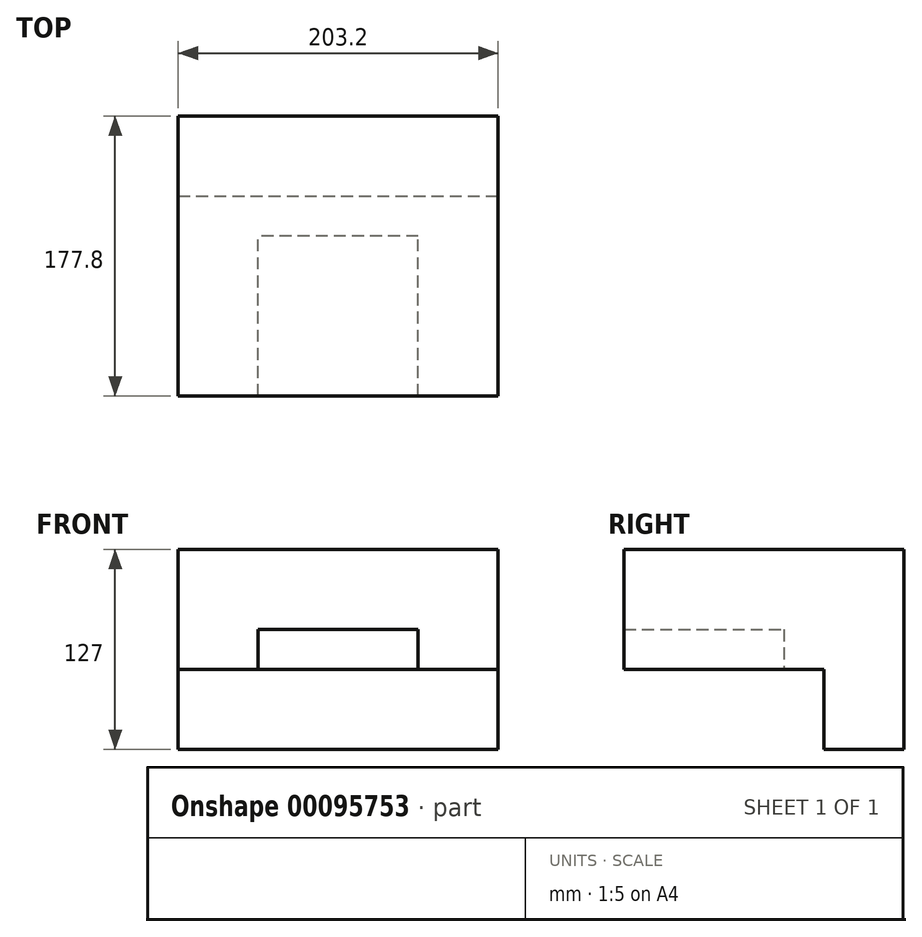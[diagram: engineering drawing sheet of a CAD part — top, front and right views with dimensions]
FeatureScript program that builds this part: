
annotation { "Feature Type Name" : "Feature", "Feature Type Description" : "" }
export const myFeature = defineFeature(function(context is Context, id is Id, definition is map)
    precondition{}
    {
        {
            var Q0;
            Q0=qCreatedBy(makeId("Front.planeOp"),FACE);
            var sketch = newSketch(context, id + "F0", { "sketchPlane" : qUnion([Q0])});
            skLineSegment(sketch, "E0.bottom", {"start": v(-127.89, 75.16) * mm, "end": v(75.31, 75.16) * mm});
            skLineSegment(sketch, "E0.top", {"start": v(-127.89, -51.84) * mm, "end": v(75.31, -51.84) * mm});
            skLineSegment(sketch, "E0.left", {"start": v(-127.89, 75.16) * mm, "end": v(-127.89, -51.84) * mm});
            skLineSegment(sketch, "E0.right", {"start": v(75.31, 75.16) * mm, "end": v(75.31, -51.84) * mm});
            skSolve(sketch);
        }
        {
            var Q0;
            Q0 = qSketchRegion(id + "F0", true);
            extrude(context, id + "F1", {"entities" : qUnion([Q0]), "depth" : 50.8 * mm});
        }
        {
            var Q0;
            Q0=makeQuery(id+"F1.opExtrude","CAP_FACE",FACE,{"disambiguationData":[OSD([sQuery(id+"F0.wireOp",EDGE,"E0.bottom"),sQuery(id+"F0.wireOp",EDGE,"E0.top"),sQuery(id+"F0.wireOp",EDGE,"E0.left"),sQuery(id+"F0.wireOp",EDGE,"E0.right")])],"isStart":false});
            var sketch = newSketch(context, id + "F2", { "sketchPlane" : qUnion([Q0])});
            skLineSegment(sketch, "E1", {"start": v(-127.89, -1.04) * mm, "end": v(75.31, -1.04) * mm});
            skLineSegment(sketch, "E2.bottom", {"start": v(-127.89, 75.16) * mm, "end": v(75.31, 75.16) * mm});
            skLineSegment(sketch, "E2.left", {"start": v(-127.89, 75.16) * mm, "end": v(-127.89, -1.04) * mm});
            skLineSegment(sketch, "E2.right", {"start": v(75.31, 75.16) * mm, "end": v(75.31, -1.04) * mm});
            skSolve(sketch);
        }
        {
            var Q0;
            Q0 = qSketchRegion(id + "F2", true);
            extrude(context, id + "F3", {"entities" : qUnion([Q0]), "operationType" : NewBodyOperationType.ADD, "depth" : 25.4 * mm});
        }
        {
            var Q0;
            Q0=makeQuery(id+"F3.opExtrude","CAP_FACE",FACE,{"disambiguationData":[OSD([sQuery(id+"F2.wireOp",EDGE,"E2.bottom"),sQuery(id+"F2.wireOp",EDGE,"E1"),sQuery(id+"F2.wireOp",EDGE,"E2.left"),sQuery(id+"F2.wireOp",EDGE,"E2.right")])],"isStart":false});
            var sketch = newSketch(context, id + "F4", { "sketchPlane" : qUnion([Q0])});
            skLineSegment(sketch, "E3.bottom", {"start": v(24.51, 24.36) * mm, "end": v(-77.09, 24.36) * mm});
            skLineSegment(sketch, "E3.left", {"start": v(24.51, 24.36) * mm, "end": v(24.51, -1.04) * mm});
            skLineSegment(sketch, "E4", {"start": v(-127.89, -1.04) * mm, "end": v(-77.09, -1.04) * mm});
            skLineSegment(sketch, "E5", {"start": v(24.51, -1.04) * mm, "end": v(75.31, -1.04) * mm});
            skLineSegment(sketch, "E6", {"start": v(75.31, -1.04) * mm, "end": v(75.31, 75.16) * mm});
            skLineSegment(sketch, "E7", {"start": v(75.31, 75.16) * mm, "end": v(-127.89, 75.16) * mm});
            skLineSegment(sketch, "E8", {"start": v(-127.89, 75.16) * mm, "end": v(-127.89, -1.04) * mm});
            skLineSegment(sketch, "E9", {"start": v(-77.09, 24.36) * mm, "end": v(-77.09, -1.04) * mm});
            skSolve(sketch);
        }
        {
            var Q0;
            Q0 = qSketchRegion(id + "F4", true);
            extrude(context, id + "F5", {"entities" : qUnion([Q0]), "operationType" : NewBodyOperationType.ADD, "depth" : 101.6 * mm});
        }
    });
